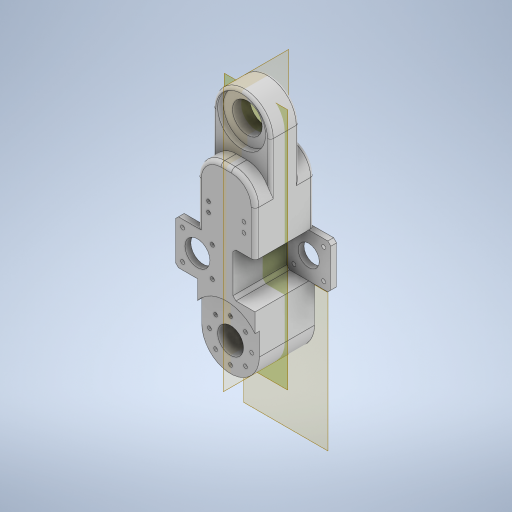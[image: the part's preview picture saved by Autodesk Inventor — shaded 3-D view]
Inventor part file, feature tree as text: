
AUTODESK INVENTOR PART (.ipt)
format: ipt  version: 2024 (Build 280153000, 153)  size: 1,355,264 bytes
history: native  units: mm
features: extrude x13, sketch x12, reference x8, other x7, fillet x5, plane x4, mirror x4, projected_geometry x4
ambient origin geometry x8: Origin, YZ Plane, XZ Plane, XY Plane, X Axis, Y Axis, Z Axis, Center Point
bodies: Solid1 (feature_tree)
feature tree (57):
  plane  "Work Plane1"
  other  "main"
  plane  "Work Plane2"
  extrude  "main extrude"  Depth=10.0mm TaperAngle=0.0deg
  other  "midplane"
  mirror  "right motor"
  extrude  "screwholes"  Depth=60.0mm
  extrude  "arm joint"  Depth=10.0mm TaperAngle=0.0deg
  extrude  "bearing hole"  Depth=60.0mm
  extrude  "axle hole"  TaperAngle=0.0deg  [1 undecoded]
  mirror  "Mirror3"
  fillet  "Fillet1"  Radius=38.0mm
  fillet  "Fillet3"  Radius=27.0mm
  mirror  "Mirror4"
  extrude  "Extrusion12"  Depth=6.0mm TaperAngle=0.0deg
  extrude  "Extrusion14"  TaperAngle=0.0deg  [1 undecoded]
  extrude  "Extrusion15"  Depth=30.0mm
  extrude  "Extrusion16"  TaperAngle=0.0deg  [1 undecoded]
  fillet  "Fillet5"  Radius=2.0mm
  fillet  "Fillet6"  Radius=6.0mm
  fillet  "Fillet7"  Radius=2.0mm
  extrude  "Extrusion17"  Depth=2.0mm
  extrude  "Extrusion18"  Depth=2.0mm
  extrude  "Extrusion19"  Depth=2.0mm
  plane  "Work Plane6"
  mirror  "Mirror5"
  extrude  "Extrusion20"  Depth=2.0mm
  reference  "Reference1"
  reference  "Reference2"
  reference  "Reference3"
  reference  "Reference4"
  plane  "Work Plane5"
  sketch  "Sketch7"  dims[d0=60.0mm d1=10.0mm d2=0.0mm]
  sketch  "Sketch8"  dims[d4=160.0mm d5=60.0mm]
  projected_geometry  "Projected Loop3"
  sketch  "Sketch10"  dims[d6=30.0mm d36=10.0mm d37=0.0mm]
  projected_geometry  "Projected Loop4"
  sketch  "Sketch11"  dims[d39=15.0mm d40=60.0mm]
  projected_geometry  "Projected Loop5"
  sketch  "Sketch14"  dims[d41=15.0mm d43=0.0mm d44=0.0mm d45=38.0mm d46=27.0mm]
  reference  "Reference8"
  sketch  "Sketch17"  dims[d47=6.0mm d48=6.0mm d49=0.0mm]
  reference  "Reference10"
  sketch  "Sketch18"  dims[d50=27.0mm d51=0.0mm d52=0.0mm]
  reference  "Reference13"
  sketch  "Sketch19"  dims[d53=30.0mm d59=24.5mm]
  reference  "Reference14"
  sketch  "Sketch20"  dims[d65=2.0mm d66=0.0mm d67=0.0mm d72=2.0mm d73=6.0mm d74=0.0mm d84=2.0mm]
  sketch  "Sketch21"  dims[d85=2.0mm d86=4.2mm]
  sketch  "Sketch22"  dims[d87=6.0mm d88=0.0mm d89=2.0mm]
  sketch  "Sketch23"  dims[d90=2.0mm d91=4.2mm d92=4.2mm d93=4.2mm d94=4.2mm d95=6.0mm d96=0.0mm d97=4.0mm d98=3.0mm d99=4.0mm d100=1.0mm d101=0.0mm d102=3.9mm d103=3.9mm d104=10.0mm d105=45.278655mm d106=11.56547mm d107=0.0mm d108=0.0mm d109=8.0mm d110=4.5mm d111=0.0mm d112=2.0mm d113=0.0mm d114=0.0mm d80=0.5mm d81=0.872665mm d82=0.5mm d83=0.872665mm]
  projected_geometry  "Projected Loop8"
  other  "<userpath>\Documents\Inventor\robot arm\arms\arms.iam"
  other  "arms.iam"
  other  "base:1"
  other  "stepper motor:2"
  other  "stepper motor:1"
note: 3 required parameter values undecoded (feature->parameter linkage not recoverable at this tier; creation-order binding heuristic only, values carry confidence <= 0.55)
